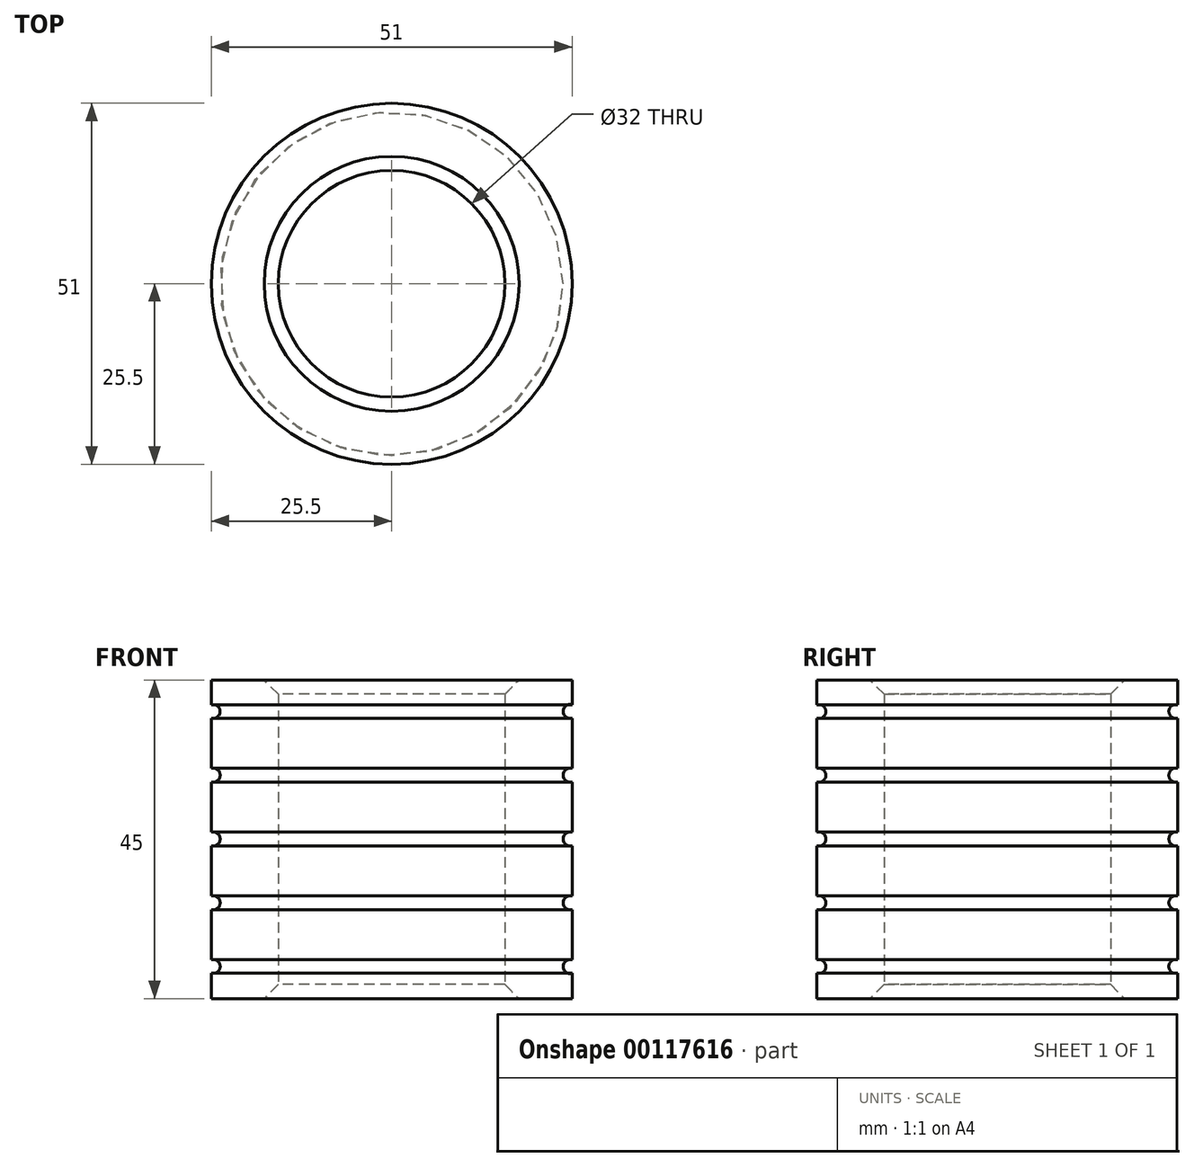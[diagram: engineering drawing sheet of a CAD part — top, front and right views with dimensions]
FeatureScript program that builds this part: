
annotation { "Feature Type Name" : "Feature", "Feature Type Description" : "" }
export const myFeature = defineFeature(function(context is Context, id is Id, definition is map)
    precondition{}
    {
        {
            var Q0;
            Q0=qCreatedBy(makeId("Top.planeOp"),FACE);
            var sketch = newSketch(context, id + "F0", { "sketchPlane" : qUnion([Q0])});
            skCircle(sketch, "E0", {"center": v(0, 0) * mm, "radius": 25.5 * mm});
            skCircle(sketch, "E1", {"center": v(0, 0) * mm, "radius": 16 * mm});
            skSolve(sketch);
        }
        {
            var Q0;
            Q0 = qSketchRegion(id + "F0", true);
            extrude(context, id + "F1", {"entities" : qUnion([Q0]), "depth" : 45 * mm});
        }
        {
            var Q0;
            Q0=makeQuery(id+"F1.opExtrude","CAP_EDGE",EDGE,{"disambiguationData":[OSD([sQuery(id+"F0.wireOp",EDGE,"E1")])],"isStart":false});
            var Q1;
            Q1=makeQuery(id+"F1.opExtrude","CAP_EDGE",EDGE,{"disambiguationData":[OSD([sQuery(id+"F0.wireOp",EDGE,"E1")])],"isStart":true});
            chamfer(context, id + "F2", {"entities" : qUnion([Q0, Q1]), "width" : 2 * mm, "tangentPropagation" : true});
        }
        {
            var Q0;
            Q0=qCreatedBy(makeId("Front.planeOp"),FACE);
            var sketch = newSketch(context, id + "F3", { "sketchPlane" : qUnion([Q0])});
            skLineSegment(sketch, "E2", {"start": v(-25.23, 45.07) * mm, "end": v(-25.23, 0) * mm, "construction": true});
            skCircle(sketch, "E3", {"center": v(-25.23, 40.57) * mm, "radius": 1 * mm});
            skCircle(sketch, "E4.1.0.0", {"center": v(-25.23, 31.56) * mm, "radius": 1 * mm});
            skCircle(sketch, "E4.2.0.0", {"center": v(-25.23, 22.55) * mm, "radius": 1 * mm});
            skCircle(sketch, "E4.3.0.0", {"center": v(-25.23, 13.54) * mm, "radius": 1 * mm});
            skCircle(sketch, "E4.4.0.0", {"center": v(-25.22, 4.53) * mm, "radius": 1 * mm});
            skLineSegment(sketch, "E4.direction1", {"start": v(-25.23, 40.57) * mm, "end": v(-25.23, 31.56) * mm, "construction": true});
            skLineSegment(sketch, "E5", {"start": v(0, 0) * mm, "end": v(0, 60.55) * mm, "construction": true});
            skSolve(sketch);
        }
        {
            var Q0;
            Q0 = qSketchRegion(id + "F3", true);
            var Q1;
            Q1=sQuery(id+"F3.wireOp",EDGE,"E5");
            revolve(context, id + "F4", {"operationType" : NewBodyOperationType.REMOVE, "entities" : qUnion([Q0]), "axis" : qUnion([Q1]), "revolveType" : RevolveType.FULL, "oppositeDirection" : true});
        }
    });
